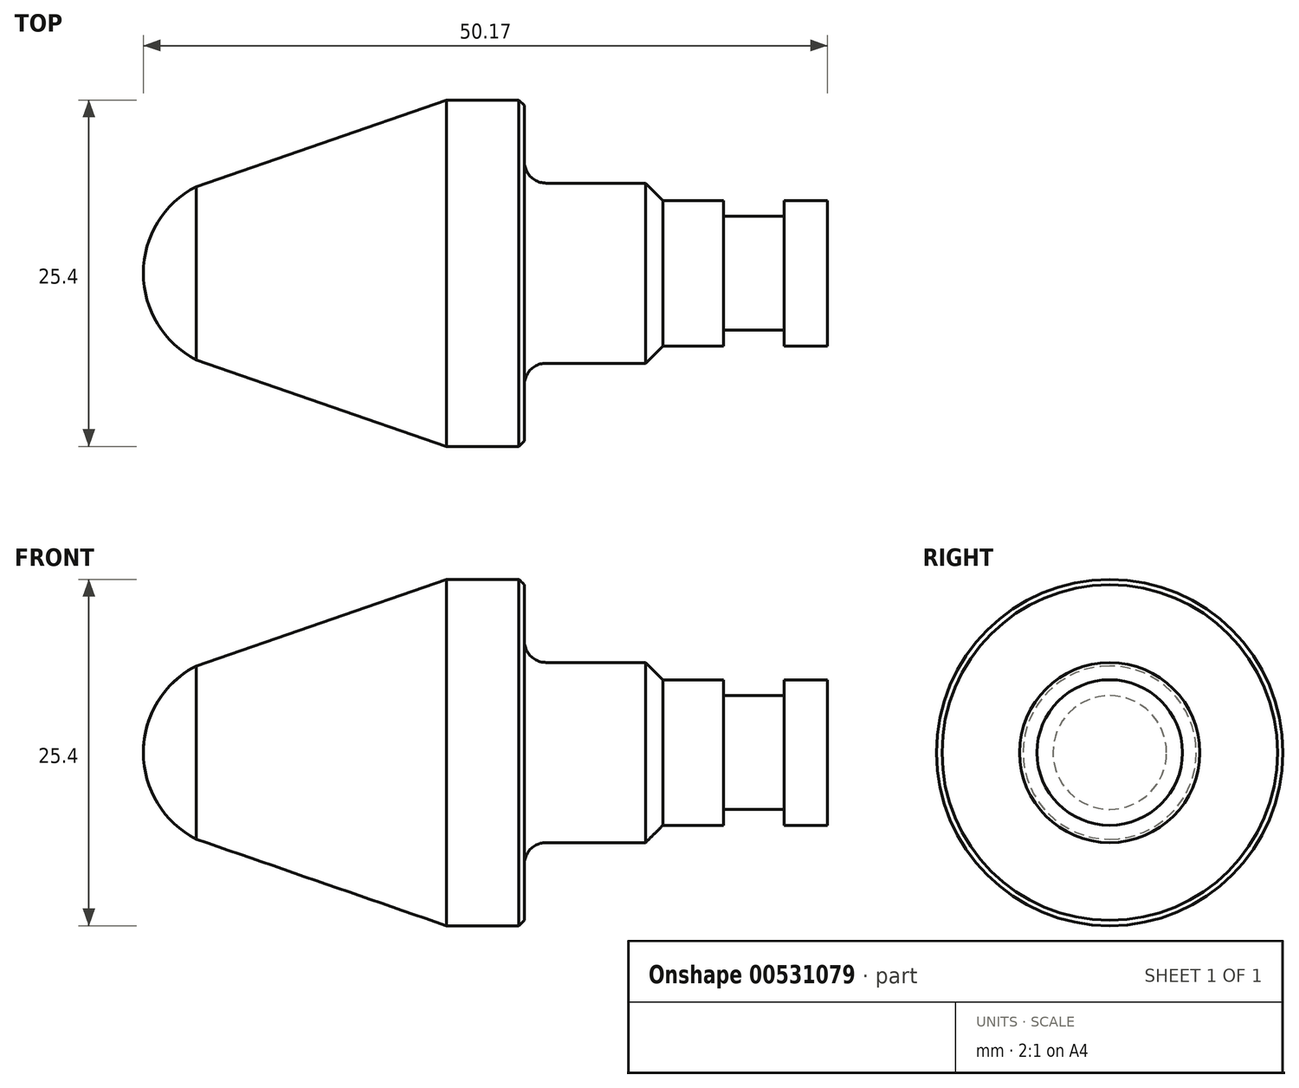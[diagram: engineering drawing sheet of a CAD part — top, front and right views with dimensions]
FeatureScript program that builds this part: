
annotation { "Feature Type Name" : "Feature", "Feature Type Description" : "" }
export const myFeature = defineFeature(function(context is Context, id is Id, definition is map)
    precondition{}
    {
        {
            var Q0;
            Q0=qCreatedBy(makeId("Front.planeOp"),FACE);
            var sketch = newSketch(context, id + "F0", { "sketchPlane" : qUnion([Q0])});
            skLineSegment(sketch, "E0", {"start": v(0, 12.7) * mm, "end": v(-5.72, 12.7) * mm});
            skLineSegment(sketch, "E1", {"start": v(-5.72, 12.7) * mm, "end": v(-24.07, 6.35) * mm});
            skLineSegment(sketch, "E2", {"start": v(0, 12.7) * mm, "end": v(0, 8.2) * mm});
            skLineSegment(sketch, "E3", {"start": v(1.59, 6.6) * mm, "end": v(8.9, 6.6) * mm});
            skLineSegment(sketch, "E4", {"start": v(8.9, 6.6) * mm, "end": v(10.16, 5.33) * mm});
            skLineSegment(sketch, "E5", {"start": v(10.16, 5.33) * mm, "end": v(14.6, 5.33) * mm});
            skLineSegment(sketch, "E6", {"start": v(14.6, 5.33) * mm, "end": v(14.6, 4.17) * mm});
            skLineSegment(sketch, "E7", {"start": v(14.6, 4.17) * mm, "end": v(19.05, 4.17) * mm});
            skLineSegment(sketch, "E8", {"start": v(19.05, 4.17) * mm, "end": v(19.05, 5.33) * mm});
            skLineSegment(sketch, "E9", {"start": v(19.05, 5.33) * mm, "end": v(22.23, 5.33) * mm});
            skLineSegment(sketch, "E10", {"start": v(22.23, 5.33) * mm, "end": v(22.23, 0) * mm});
            skPoint(sketch, "E11.visualSharp", {"position": v(0, 6.6) * mm});
            skArc(sketch, "E11.filletArc", {"start": v(0, 8.2) * mm, "mid": v(0.46, 7.07) * mm, "end": v(1.59, 6.6) * mm});
            skArc(sketch, "E12", {"start": v(-24.07, 6.35) * mm, "mid": v(-26.9, 3.72) * mm, "end": v(-27.94, 0) * mm});
            skLineSegment(sketch, "E13", {"start": v(-27.94, 0) * mm, "end": v(-27.94, 6.35) * mm, "construction": true});
            skLineSegment(sketch, "E14", {"start": v(22.23, 0) * mm, "end": v(-27.94, 0) * mm});
            skSolve(sketch);
        }
        {
            var Q0;
            Q0=makeQuery(id+"F0.imprint","IMPRINT",FACE,{"disambiguationData":[TD([[makeQuery(id+"F0.imprint","IMPRINT",EDGE,{"derivedFrom":sQuery(id+"F0.wireOp",EDGE,"MaEDnVJF-N6Ds-aKYR-kCXn-q3KZAcvYysNf")}),1.0]])]});
            var Q1;
            Q1=makeQuery(id+"F0.imprint","IMPRINT",FACE,{"disambiguationData":[TD([[makeQuery(id+"F0.imprint","IMPRINT",EDGE,{"derivedFrom":sQuery(id+"F0.wireOp",EDGE,"E0")}),1.0]])]});
            var Q2;
            Q2=sQuery(id+"F0.wireOp",EDGE,"E14");
            revolve(context, id + "F1", {"entities" : qUnion([Q0, Q1]), "axis" : qUnion([Q2]), "revolveType" : RevolveType.FULL});
        }
        {
            var Q0;
            Q0=makeQuery(id+"F1.opRevolve","SWEPT_EDGE",EDGE,{"disambiguationData":[OSD([sQuery(id+"F0.wireOp",EDGE,"E0"),sQuery(id+"F0.wireOp",EDGE,"E2")])]});
            chamfer(context, id + "F2", {"entities" : qUnion([Q0]), "width" : 0.4 * mm, "tangentPropagation" : true});
        }
    });
